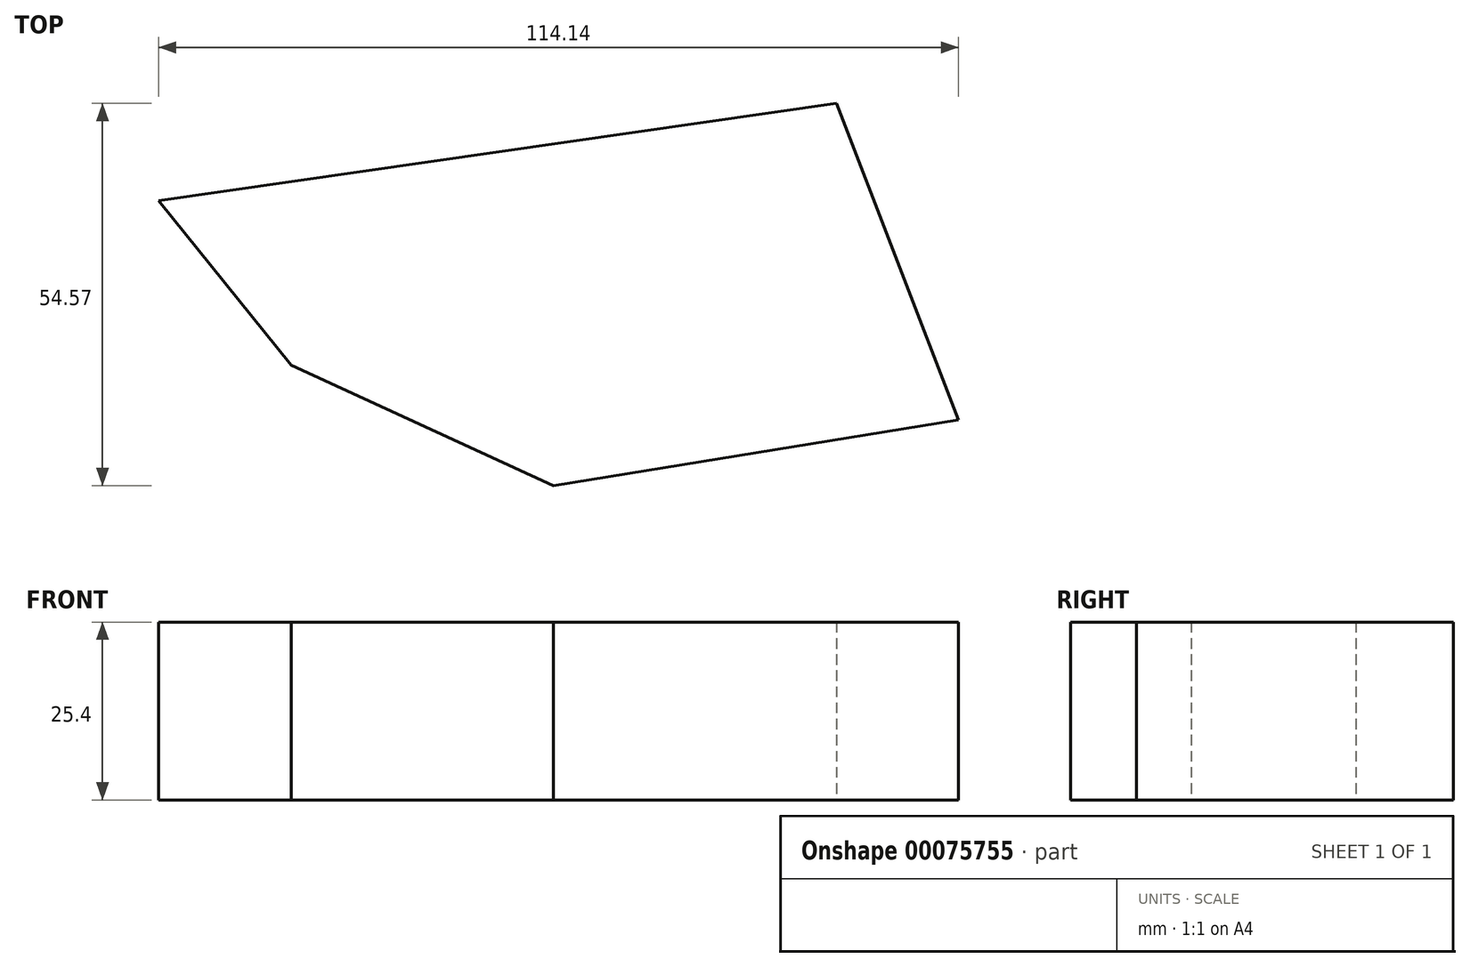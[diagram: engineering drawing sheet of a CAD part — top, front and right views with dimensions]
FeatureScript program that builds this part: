
annotation { "Feature Type Name" : "Feature", "Feature Type Description" : "" }
export const myFeature = defineFeature(function(context is Context, id is Id, definition is map)
    precondition{}
    {
        {
            var Q0;
            Q0=qCreatedBy(makeId("Top.planeOp"),FACE);
            var sketch = newSketch(context, id + "F0", { "sketchPlane" : qUnion([Q0])});
            skLineSegment(sketch, "E0", {"start": v(-56.31, 40.66) * mm, "end": v(-37.4, 17.18) * mm});
            skLineSegment(sketch, "E1", {"start": v(-37.4, 17.18) * mm, "end": v(0, 0) * mm});
            skLineSegment(sketch, "E2", {"start": v(0, 0) * mm, "end": v(57.83, 9.35) * mm});
            skLineSegment(sketch, "E3", {"start": v(57.83, 9.35) * mm, "end": v(40.44, 54.57) * mm});
            skLineSegment(sketch, "E4", {"start": v(40.44, 54.57) * mm, "end": v(-56.31, 40.66) * mm});
            skSolve(sketch);
        }
        {
            var Q0;
            Q0=makeQuery(id+"F0.imprint","IMPRINT",FACE,{"disambiguationData":[TD([[makeQuery(id+"F0.imprint","IMPRINT",EDGE,{"derivedFrom":sQuery(id+"F0.wireOp",EDGE,"E0")}),1.0]])]});
            extrude(context, id + "F1", {"entities" : qUnion([Q0]), "depth" : 25.4 * mm});
        }
    });
